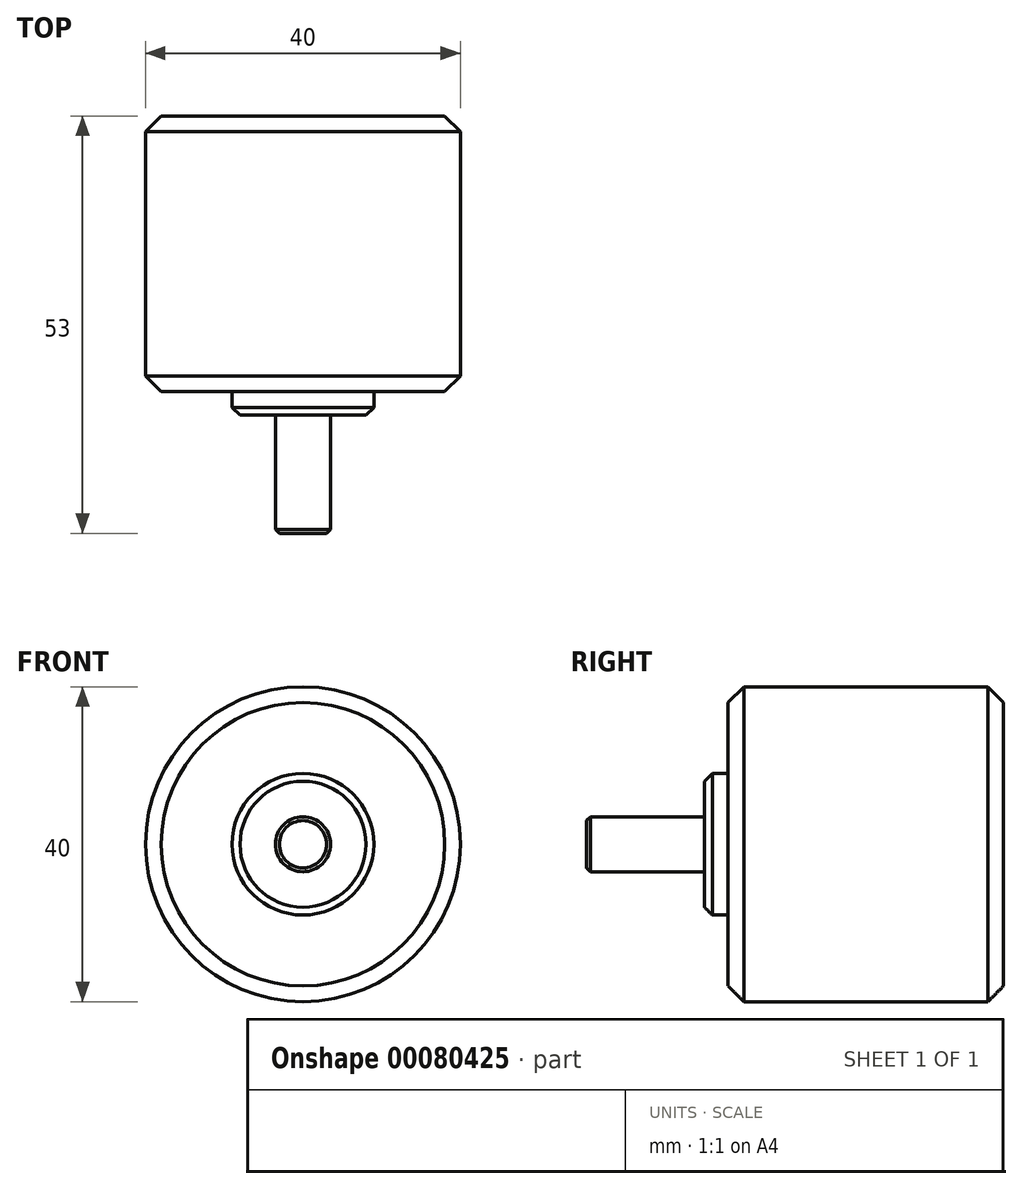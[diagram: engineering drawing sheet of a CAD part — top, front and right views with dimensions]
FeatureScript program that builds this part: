
annotation { "Feature Type Name" : "Feature", "Feature Type Description" : "" }
export const myFeature = defineFeature(function(context is Context, id is Id, definition is map)
    precondition{}
    {
        {
            var Q0;
            Q0=qCreatedBy(makeId("Front.planeOp"),FACE);
            var sketch = newSketch(context, id + "F0", { "sketchPlane" : qUnion([Q0])});
            skCircle(sketch, "E0", {"center": v(0, 0) * mm, "radius": 20 * mm});
            skSolve(sketch);
        }
        {
            var Q0;
            Q0 = qSketchRegion(id + "F0", true);
            extrude(context, id + "F1", {"entities" : qUnion([Q0]), "endBound" : BoundingType.SYMMETRIC, "depth" : 35 * mm});
        }
        {
            var Q0;
            Q0=makeQuery(id+"F1.opExtrude","CAP_EDGE",EDGE,{"disambiguationData":[OSD([sQuery(id+"F0.wireOp",EDGE,"E0")])],"isStart":true});
            var Q1;
            Q1=makeQuery(id+"F1.opExtrude","CAP_EDGE",EDGE,{"disambiguationData":[OSD([sQuery(id+"F0.wireOp",EDGE,"E0")])],"isStart":false});
            chamfer(context, id + "F2", {"entities" : qUnion([Q0, Q1]), "width" : 2 * mm, "tangentPropagation" : true});
        }
        {
            var Q0;
            Q0=makeQuery(id+"F1.opExtrude","CAP_FACE",FACE,{"disambiguationData":[OSD([sQuery(id+"F0.wireOp",EDGE,"E0")])],"isStart":false});
            var sketch = newSketch(context, id + "F3", { "sketchPlane" : qUnion([Q0])});
            skCircle(sketch, "E1", {"center": v(0, 0) * mm, "radius": 9 * mm});
            skSolve(sketch);
        }
        {
            var Q0;
            Q0 = qSketchRegion(id + "F3", true);
            extrude(context, id + "F4", {"entities" : qUnion([Q0]), "operationType" : NewBodyOperationType.ADD, "depth" : 3 * mm});
        }
        {
            var Q0;
            Q0=makeQuery(id+"F4.opExtrude","CAP_FACE",FACE,{"disambiguationData":[OSD([sQuery(id+"F3.wireOp",EDGE,"E1")])],"isStart":false});
            var sketch = newSketch(context, id + "F5", { "sketchPlane" : qUnion([Q0])});
            skCircle(sketch, "E2", {"center": v(0, 0) * mm, "radius": 3.5 * mm});
            skSolve(sketch);
        }
        {
            var Q0;
            Q0 = qSketchRegion(id + "F5", true);
            extrude(context, id + "F6", {"entities" : qUnion([Q0]), "depth" : 15 * mm});
        }
        {
            var Q0;
            Q0=makeQuery(id+"F6.opExtrude","CAP_FACE",FACE,{"disambiguationData":[OSD([sQuery(id+"F5.wireOp",EDGE,"E2")])],"isStart":false});
            chamfer(context, id + "F7", {"entities" : qUnion([Q0]), "width" : 0.5 * mm, "tangentPropagation" : true});
        }
        {
            var Q0;
            Q0=makeQuery(id+"F4.opExtrude","CAP_EDGE",EDGE,{"disambiguationData":[OSD([sQuery(id+"F3.wireOp",EDGE,"E1")])],"isStart":false});
            chamfer(context, id + "F8", {"entities" : qUnion([Q0]), "width" : 1 * mm, "tangentPropagation" : true});
        }
    });
